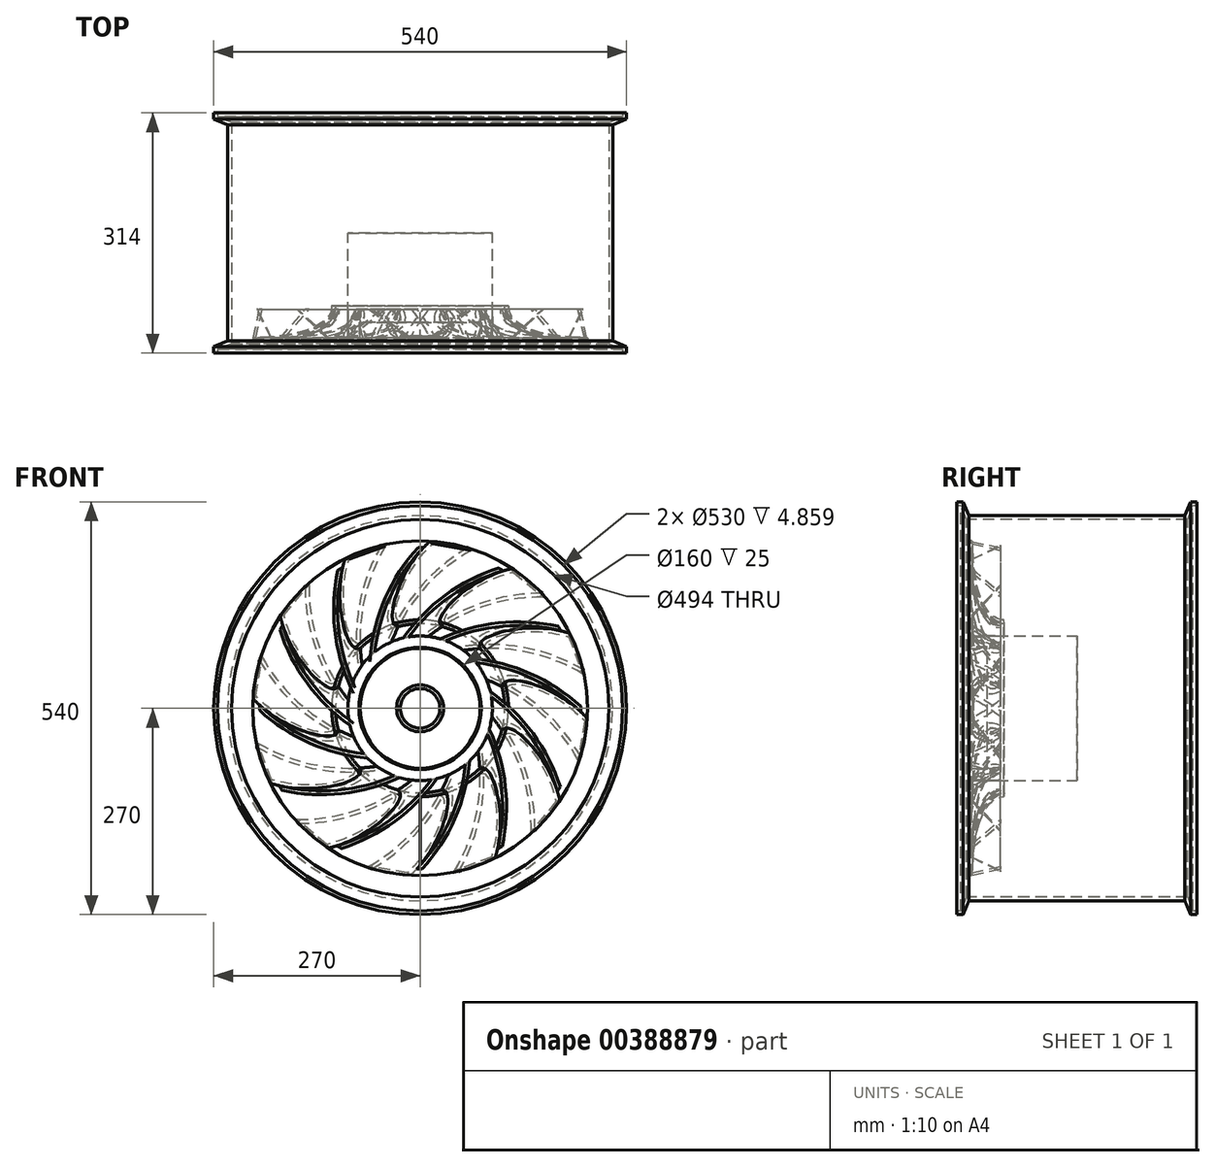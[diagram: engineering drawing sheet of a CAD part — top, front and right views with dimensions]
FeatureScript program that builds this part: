
annotation { "Feature Type Name" : "Feature", "Feature Type Description" : "" }
export const myFeature = defineFeature(function(context is Context, id is Id, definition is map)
    precondition{}
    {
        {
            var Q0;
            Q0=qCreatedBy(makeId("Right.planeOp"),FACE);
            var sketch = newSketch(context, id + "F0", { "sketchPlane" : qUnion([Q0])});
            skLineSegment(sketch, "E0", {"start": v(-157, 265) * mm, "end": v(-152.14, 265) * mm});
            skLineSegment(sketch, "E1", {"start": v(-152.14, 265) * mm, "end": v(-144.8, 247) * mm});
            skLineSegment(sketch, "E2", {"start": v(-144.8, 247) * mm, "end": v(0, 247) * mm});
            skLineSegment(sketch, "E3.0", {"start": v(-141.45, 252) * mm, "end": v(0, 252) * mm});
            skLineSegment(sketch, "E3.1", {"start": v(-148.78, 270) * mm, "end": v(-141.45, 252) * mm});
            skLineSegment(sketch, "E3.2", {"start": v(-157, 270) * mm, "end": v(-148.78, 270) * mm});
            skLineSegment(sketch, "E4", {"start": v(-157, 270) * mm, "end": v(-157, 265) * mm});
            skLineSegment(sketch, "E5", {"start": v(0, 298.63) * mm, "end": v(0, -252.46) * mm, "construction": true});
            skLineSegment(sketch, "E6", {"start": v(-294.47, 0) * mm, "end": v(276.15, 0) * mm, "construction": true});
            skLineSegment(sketch, "E7.MirrorCS", {"start": v(157, 270) * mm, "end": v(148.78, 270) * mm});
            skLineSegment(sketch, "E8.MirrorCS", {"start": v(157, 270) * mm, "end": v(157, 265) * mm});
            skLineSegment(sketch, "E9.MirrorCS", {"start": v(157, 265) * mm, "end": v(152.14, 265) * mm});
            skLineSegment(sketch, "E10.MirrorCS", {"start": v(148.78, 270) * mm, "end": v(141.45, 252) * mm});
            skLineSegment(sketch, "E11.MirrorCS", {"start": v(152.14, 265) * mm, "end": v(144.8, 247) * mm});
            skLineSegment(sketch, "E12.MirrorCS", {"start": v(144.8, 247) * mm, "end": v(0, 247) * mm});
            skLineSegment(sketch, "E13.MirrorCS", {"start": v(141.45, 252) * mm, "end": v(0, 252) * mm});
            skSolve(sketch);
        }
        {
            var Q0;
            Q0 = qSketchRegion(id + "F0", true);
            var Q1;
            Q1=sQuery(id+"F0.wireOp",EDGE,"E6");
            revolve(context, id + "F1", {"entities" : qUnion([Q0]), "axis" : qUnion([Q1]), "revolveType" : RevolveType.FULL});
        }
        {
            var Q0;
            Q0=qCreatedBy(makeId("Front.planeOp"),FACE);
            var sketch = newSketch(context, id + "F2", { "sketchPlane" : qUnion([Q0])});
            skCircle(sketch, "E14", {"center": v(0, 0) * mm, "radius": 94.6 * mm});
            skSolve(sketch);
        }
        {
            var Q0;
            Q0 = qSketchRegion(id + "F2", true);
            extrude(context, id + "F3", {"entities" : qUnion([Q0]), "depth" : 142 * mm});
        }
        {
            var Q0;
            Q0=qCreatedBy(makeId("Front.planeOp"),FACE);
            cPlane(context, id + "F4", {"entities" : qUnion([Q0]), "cplaneType" : CPlaneType.OFFSET, "offset" : 100 * mm, "width" : 150 * mm, "height" : 150 * mm});
        }
        {
            var Q0;
            Q0=qCreatedBy(id+"F4.planeOp",FACE);
            var sketch = newSketch(context, id + "F5", { "sketchPlane" : qUnion([Q0])});
            skArc(sketch, "E15", {"start": v(-55.5, 40.57) * mm, "mid": v(-15.2, 138.78) * mm, "end": v(63.24, 210.31) * mm});
            skArc(sketch, "E16.0", {"start": v(-50.14, 42.17) * mm, "mid": v(-10, 137.48) * mm, "end": v(66.9, 206.64) * mm});
            skLineSegment(sketch, "E17", {"start": v(66.9, 206.64) * mm, "end": v(63.24, 210.31) * mm});
            skLineSegment(sketch, "E18", {"start": v(-50.14, 42.17) * mm, "end": v(-55.5, 40.57) * mm});
            skLineSegment(sketch, "E19.1.0", {"start": v(-45.38, 212.4) * mm, "end": v(-50.39, 213.75) * mm});
            skArc(sketch, "E19.1.1", {"start": v(-64.5, 11.44) * mm, "mid": v(-77.4, 114.06) * mm, "end": v(-45.38, 212.4) * mm});
            skArc(sketch, "E19.1.2", {"start": v(-68.35, 7.39) * mm, "mid": v(-82.55, 112.59) * mm, "end": v(-50.39, 213.75) * mm});
            skLineSegment(sketch, "E19.1.3", {"start": v(-64.5, 11.44) * mm, "end": v(-68.35, 7.39) * mm});
            skLineSegment(sketch, "E19.2.0", {"start": v(-145.5, 161.25) * mm, "end": v(-150.52, 159.92) * mm});
            skArc(sketch, "E19.2.1", {"start": v(-61.59, -22.34) * mm, "mid": v(-124.06, 60.08) * mm, "end": v(-145.5, 161.25) * mm});
            skArc(sketch, "E19.2.2", {"start": v(-62.89, -27.78) * mm, "mid": v(-127.79, 56.23) * mm, "end": v(-150.52, 159.92) * mm});
            skLineSegment(sketch, "E19.2.3", {"start": v(-61.59, -22.34) * mm, "end": v(-62.89, -27.78) * mm});
            skLineSegment(sketch, "E19.3.0", {"start": v(-206.64, 66.9) * mm, "end": v(-210.31, 63.24) * mm});
            skArc(sketch, "E19.3.1", {"start": v(-42.17, -50.14) * mm, "mid": v(-137.48, -10) * mm, "end": v(-206.64, 66.9) * mm});
            skArc(sketch, "E19.3.2", {"start": v(-40.57, -55.5) * mm, "mid": v(-138.78, -15.2) * mm, "end": v(-210.31, 63.24) * mm});
            skLineSegment(sketch, "E19.3.3", {"start": v(-42.17, -50.14) * mm, "end": v(-40.57, -55.5) * mm});
            skLineSegment(sketch, "E19.4.0", {"start": v(-212.4, -45.38) * mm, "end": v(-213.75, -50.39) * mm});
            skArc(sketch, "E19.4.1", {"start": v(-11.44, -64.5) * mm, "mid": v(-114.06, -77.4) * mm, "end": v(-212.4, -45.38) * mm});
            skArc(sketch, "E19.4.2", {"start": v(-7.39, -68.35) * mm, "mid": v(-112.59, -82.55) * mm, "end": v(-213.75, -50.39) * mm});
            skLineSegment(sketch, "E19.4.3", {"start": v(-11.44, -64.5) * mm, "end": v(-7.39, -68.35) * mm});
            skLineSegment(sketch, "E19.5.0", {"start": v(-161.25, -145.5) * mm, "end": v(-159.92, -150.52) * mm});
            skArc(sketch, "E19.5.1", {"start": v(22.34, -61.59) * mm, "mid": v(-60.08, -124.06) * mm, "end": v(-161.25, -145.5) * mm});
            skArc(sketch, "E19.5.2", {"start": v(27.78, -62.89) * mm, "mid": v(-56.23, -127.79) * mm, "end": v(-159.92, -150.52) * mm});
            skLineSegment(sketch, "E19.5.3", {"start": v(22.34, -61.59) * mm, "end": v(27.78, -62.89) * mm});
            skLineSegment(sketch, "E19.6.0", {"start": v(-66.9, -206.64) * mm, "end": v(-63.24, -210.31) * mm});
            skArc(sketch, "E19.6.1", {"start": v(50.14, -42.17) * mm, "mid": v(10, -137.48) * mm, "end": v(-66.9, -206.64) * mm});
            skArc(sketch, "E19.6.2", {"start": v(55.5, -40.57) * mm, "mid": v(15.2, -138.78) * mm, "end": v(-63.24, -210.31) * mm});
            skLineSegment(sketch, "E19.6.3", {"start": v(50.14, -42.17) * mm, "end": v(55.5, -40.57) * mm});
            skLineSegment(sketch, "E19.7.0", {"start": v(45.38, -212.4) * mm, "end": v(50.39, -213.75) * mm});
            skArc(sketch, "E19.7.1", {"start": v(64.5, -11.44) * mm, "mid": v(77.4, -114.06) * mm, "end": v(45.38, -212.4) * mm});
            skArc(sketch, "E19.7.2", {"start": v(68.35, -7.39) * mm, "mid": v(82.55, -112.59) * mm, "end": v(50.39, -213.75) * mm});
            skLineSegment(sketch, "E19.7.3", {"start": v(64.5, -11.44) * mm, "end": v(68.35, -7.39) * mm});
            skLineSegment(sketch, "E19.8.0", {"start": v(145.5, -161.25) * mm, "end": v(150.52, -159.92) * mm});
            skArc(sketch, "E19.8.1", {"start": v(61.59, 22.34) * mm, "mid": v(124.06, -60.08) * mm, "end": v(145.5, -161.25) * mm});
            skArc(sketch, "E19.8.2", {"start": v(62.89, 27.78) * mm, "mid": v(127.79, -56.23) * mm, "end": v(150.52, -159.92) * mm});
            skLineSegment(sketch, "E19.8.3", {"start": v(61.59, 22.34) * mm, "end": v(62.89, 27.78) * mm});
            skLineSegment(sketch, "E19.9.0", {"start": v(206.64, -66.9) * mm, "end": v(210.31, -63.24) * mm});
            skArc(sketch, "E19.9.1", {"start": v(42.17, 50.14) * mm, "mid": v(137.48, 10) * mm, "end": v(206.64, -66.9) * mm});
            skArc(sketch, "E19.9.2", {"start": v(40.57, 55.5) * mm, "mid": v(138.78, 15.2) * mm, "end": v(210.31, -63.24) * mm});
            skLineSegment(sketch, "E19.9.3", {"start": v(42.17, 50.14) * mm, "end": v(40.57, 55.5) * mm});
            skLineSegment(sketch, "E19.10.0", {"start": v(212.4, 45.38) * mm, "end": v(213.75, 50.39) * mm});
            skArc(sketch, "E19.10.1", {"start": v(11.44, 64.5) * mm, "mid": v(114.06, 77.4) * mm, "end": v(212.4, 45.38) * mm});
            skArc(sketch, "E19.10.2", {"start": v(7.39, 68.35) * mm, "mid": v(112.59, 82.55) * mm, "end": v(213.75, 50.39) * mm});
            skLineSegment(sketch, "E19.10.3", {"start": v(11.44, 64.5) * mm, "end": v(7.39, 68.35) * mm});
            skLineSegment(sketch, "E19.11.0", {"start": v(161.25, 145.5) * mm, "end": v(159.92, 150.52) * mm});
            skArc(sketch, "E19.11.1", {"start": v(-22.34, 61.59) * mm, "mid": v(60.08, 124.06) * mm, "end": v(161.25, 145.5) * mm});
            skArc(sketch, "E19.11.2", {"start": v(-27.78, 62.89) * mm, "mid": v(56.23, 127.79) * mm, "end": v(159.92, 150.52) * mm});
            skLineSegment(sketch, "E19.11.3", {"start": v(-22.34, 61.59) * mm, "end": v(-27.78, 62.89) * mm});
            skPoint(sketch, "E19.center", {"position": v(0, 0) * mm});
            skSolve(sketch);
        }
        {
            var Q0;
            Q0=makeQuery(id+"F3.opExtrude","CAP_FACE",FACE,{"disambiguationData":[OSD([sQuery(id+"F2.wireOp",EDGE,"E14")])],"isStart":false});
            var sketch = newSketch(context, id + "F6", { "sketchPlane" : qUnion([Q0])});
            skArc(sketch, "E20", {"start": v(-43.6, 52.71) * mm, "mid": v(20.74, 137.14) * mm, "end": v(115.02, 185.93) * mm});
            skArc(sketch, "E21.0", {"start": v(-38.02, 52.86) * mm, "mid": v(25.42, 134.54) * mm, "end": v(117.6, 181.44) * mm});
            skLineSegment(sketch, "E22", {"start": v(117.6, 181.44) * mm, "end": v(115.02, 185.93) * mm});
            skLineSegment(sketch, "E23", {"start": v(-38.02, 52.86) * mm, "end": v(-43.6, 52.71) * mm});
            skLineSegment(sketch, "E24.1.0", {"start": v(10.64, 216.07) * mm, "end": v(6.15, 218.67) * mm});
            skArc(sketch, "E24.1.1", {"start": v(-59.85, 26.9) * mm, "mid": v(-45.74, 129.36) * mm, "end": v(10.64, 216.07) * mm});
            skArc(sketch, "E24.1.2", {"start": v(-64.6, 23.98) * mm, "mid": v(-51.1, 129.27) * mm, "end": v(6.15, 218.67) * mm});
            skLineSegment(sketch, "E24.1.3", {"start": v(-59.85, 26.9) * mm, "end": v(-64.6, 23.98) * mm});
            skLineSegment(sketch, "E24.2.0", {"start": v(-99.3, 192.57) * mm, "end": v(-104.5, 192.58) * mm});
            skArc(sketch, "E24.2.1", {"start": v(-65.77, -6.49) * mm, "mid": v(-104.78, 89.3) * mm, "end": v(-99.3, 192.57) * mm});
            skArc(sketch, "E24.2.2", {"start": v(-68.43, -11.4) * mm, "mid": v(-109.38, 86.54) * mm, "end": v(-104.5, 192.58) * mm});
            skLineSegment(sketch, "E24.2.3", {"start": v(-65.77, -6.49) * mm, "end": v(-68.43, -11.4) * mm});
            skLineSegment(sketch, "E24.3.0", {"start": v(-182.78, 117.26) * mm, "end": v(-187.28, 114.67) * mm});
            skArc(sketch, "E24.3.1", {"start": v(-54.2, -38.37) * mm, "mid": v(-135.88, 25.08) * mm, "end": v(-182.78, 117.26) * mm});
            skArc(sketch, "E24.3.2", {"start": v(-54.05, -43.95) * mm, "mid": v(-138.49, 20.4) * mm, "end": v(-187.28, 114.67) * mm});
            skLineSegment(sketch, "E24.3.3", {"start": v(-54.2, -38.37) * mm, "end": v(-54.05, -43.95) * mm});
            skLineSegment(sketch, "E24.4.0", {"start": v(-217.41, 10.3) * mm, "end": v(-220.01, 5.8) * mm});
            skArc(sketch, "E24.4.1", {"start": v(-28.25, -60.2) * mm, "mid": v(-130.7, -46.09) * mm, "end": v(-217.41, 10.3) * mm});
            skArc(sketch, "E24.4.2", {"start": v(-25.33, -64.95) * mm, "mid": v(-130.62, -51.45) * mm, "end": v(-220.01, 5.8) * mm});
            skLineSegment(sketch, "E24.4.3", {"start": v(-28.25, -60.2) * mm, "end": v(-25.33, -64.95) * mm});
            skLineSegment(sketch, "E24.5.0", {"start": v(-193.92, -99.66) * mm, "end": v(-193.93, -104.84) * mm});
            skArc(sketch, "E24.5.1", {"start": v(5.14, -66.12) * mm, "mid": v(-90.64, -105.13) * mm, "end": v(-193.92, -99.66) * mm});
            skArc(sketch, "E24.5.2", {"start": v(10.06, -68.78) * mm, "mid": v(-87.89, -109.73) * mm, "end": v(-193.93, -104.84) * mm});
            skLineSegment(sketch, "E24.5.3", {"start": v(5.14, -66.12) * mm, "end": v(10.06, -68.78) * mm});
            skLineSegment(sketch, "E24.6.0", {"start": v(-118.6, -183.13) * mm, "end": v(-116.02, -187.62) * mm});
            skArc(sketch, "E24.6.1", {"start": v(37.02, -54.55) * mm, "mid": v(-26.42, -136.23) * mm, "end": v(-118.6, -183.13) * mm});
            skArc(sketch, "E24.6.2", {"start": v(42.6, -54.4) * mm, "mid": v(-21.74, -138.83) * mm, "end": v(-116.02, -187.62) * mm});
            skLineSegment(sketch, "E24.6.3", {"start": v(37.02, -54.55) * mm, "end": v(42.6, -54.4) * mm});
            skLineSegment(sketch, "E24.7.0", {"start": v(-11.64, -217.76) * mm, "end": v(-7.15, -220.36) * mm});
            skArc(sketch, "E24.7.1", {"start": v(58.85, -28.6) * mm, "mid": v(44.74, -131.05) * mm, "end": v(-11.64, -217.76) * mm});
            skArc(sketch, "E24.7.2", {"start": v(63.61, -25.67) * mm, "mid": v(50.1, -130.96) * mm, "end": v(-7.15, -220.36) * mm});
            skLineSegment(sketch, "E24.7.3", {"start": v(58.85, -28.6) * mm, "end": v(63.61, -25.67) * mm});
            skLineSegment(sketch, "E24.8.0", {"start": v(98.31, -194.26) * mm, "end": v(103.5, -194.27) * mm});
            skArc(sketch, "E24.8.1", {"start": v(64.77, 4.8) * mm, "mid": v(103.78, -90.99) * mm, "end": v(98.31, -194.26) * mm});
            skArc(sketch, "E24.8.2", {"start": v(67.44, 9.7) * mm, "mid": v(108.38, -88.23) * mm, "end": v(103.5, -194.27) * mm});
            skLineSegment(sketch, "E24.8.3", {"start": v(64.77, 4.8) * mm, "end": v(67.44, 9.7) * mm});
            skLineSegment(sketch, "E24.9.0", {"start": v(181.78, -118.95) * mm, "end": v(186.28, -116.36) * mm});
            skArc(sketch, "E24.9.1", {"start": v(53.2, 36.68) * mm, "mid": v(134.88, -26.77) * mm, "end": v(181.78, -118.95) * mm});
            skArc(sketch, "E24.9.2", {"start": v(53.06, 42.26) * mm, "mid": v(137.49, -22.08) * mm, "end": v(186.28, -116.36) * mm});
            skLineSegment(sketch, "E24.9.3", {"start": v(53.2, 36.68) * mm, "end": v(53.06, 42.26) * mm});
            skLineSegment(sketch, "E24.10.0", {"start": v(216.41, -11.98) * mm, "end": v(219.01, -7.5) * mm});
            skArc(sketch, "E24.10.1", {"start": v(27.25, 58.5) * mm, "mid": v(129.7, 44.4) * mm, "end": v(216.41, -11.98) * mm});
            skArc(sketch, "E24.10.2", {"start": v(24.33, 63.27) * mm, "mid": v(129.62, 49.76) * mm, "end": v(219.01, -7.5) * mm});
            skLineSegment(sketch, "E24.10.3", {"start": v(27.25, 58.5) * mm, "end": v(24.33, 63.27) * mm});
            skLineSegment(sketch, "E24.11.0", {"start": v(192.92, 97.97) * mm, "end": v(192.93, 103.15) * mm});
            skArc(sketch, "E24.11.1", {"start": v(-6.14, 64.43) * mm, "mid": v(89.64, 103.44) * mm, "end": v(192.92, 97.97) * mm});
            skArc(sketch, "E24.11.2", {"start": v(-11.05, 67.09) * mm, "mid": v(86.89, 108.04) * mm, "end": v(192.93, 103.15) * mm});
            skLineSegment(sketch, "E24.11.3", {"start": v(-6.14, 64.43) * mm, "end": v(-11.05, 67.09) * mm});
            skPoint(sketch, "E24.center", {"position": v(-0.5, -0.84) * mm});
            skSolve(sketch);
        }
        {
            var Q1;
            {var subQ0=sQuery(id+"F6.wireOp",EDGE,"E24.2.0");Q1=makeQuery(id+"F6.imprint","IMPRINT",FACE,{"disambiguationData":[TD([[makeQuery(id+"F6.imprint","IMPRINT",EDGE,{"derivedFrom":subQ0}),1.0]])]});}
            var Q2;
            Q2=makeQuery(id+"F5.imprint","IMPRINT",FACE,{"disambiguationData":[TD([[makeQuery(id+"F5.imprint","IMPRINT",EDGE,{"derivedFrom":sQuery(id+"F5.wireOp",EDGE,"E19.1.0")}),1.0]])]});
            loft(context, id + "F7", {"sheetProfilesArray" : [{ "sheetProfileEntities" : qUnion([Q1]) }, { "sheetProfileEntities" : qUnion([Q2]) }]});
        }
        {
            var Q0;
            {var subQ0=sQuery(id+"F6.wireOp",EDGE,"E24.2.0");Q0=makeQuery(id+"F7.opLoft","SWEPT_BODY",BODY,{"disambiguationData":[OSD([makeQuery(id+"F5.imprint","IMPRINT",FACE,{"disambiguationData":[TD([[makeQuery(id+"F5.imprint","IMPRINT",EDGE,{"derivedFrom":sQuery(id+"F5.wireOp",EDGE,"E19.1.0")}),1.0]])]}),makeQuery(id+"F6.imprint","IMPRINT",FACE,{"disambiguationData":[TD([[makeQuery(id+"F6.imprint","IMPRINT",EDGE,{"derivedFrom":subQ0}),1.0]])]})])]});}
            var Q1;
            Q1=sQuery(id+"F0.wireOp",EDGE,"E6");
            circularPattern(context, id + "F8", {"operationType" : NewBodyOperationType.ADD, "entities" : qUnion([Q0]), "axis" : qUnion([Q1]), "angle" : 360 * degree, "instanceCount" : 12, "equalSpace" : true, "computeTransformsWithoutBuiltin" : true});
        }
        {
            var Q0;
            Q0=qCreatedBy(makeId("Right.planeOp"),FACE);
            var sketch = newSketch(context, id + "F9", { "sketchPlane" : qUnion([Q0])});
            skFitSpline(sketch, "E25", {"points": [v(-142.34, 219.16) * mm, v(-95.31, 110.7) * mm], "startDerivative": vector(5.55, -196.37) * mm, "endDerivative": vector(88.39, 0.05) * mm});
            skFitSpline(sketch, "E26.0", {"points": [v(-137.35, 219.3) * mm, v(-137.12, 211.21) * mm, v(-136.23, 195.75) * mm, v(-133.63, 174.97) * mm, v(-129.79, 156.87) * mm, v(-124.75, 141.74) * mm, v(-119.63, 131.87) * mm, v(-115.1, 125.73) * mm, v(-111.52, 122.01) * mm, v(-107.79, 119.18) * mm, v(-103.9, 117.18) * mm, v(-99.8, 115.98) * mm, v(-96.85, 115.7) * mm, v(-95.32, 115.7) * mm]});
            skLineSegment(sketch, "E27", {"start": v(-137.34, 219.02) * mm, "end": v(-142.34, 219.16) * mm});
            skLineSegment(sketch, "E28", {"start": v(-95.31, 110.7) * mm, "end": v(-95.5, 115.7) * mm});
            skSolve(sketch);
        }
        {
            var Q0;
            Q0 = qSketchRegion(id + "F9", true);
            var Q1;
            Q1=sQuery(id+"F0.wireOp",EDGE,"E6");
            revolve(context, id + "F10", {"operationType" : NewBodyOperationType.ADD, "entities" : qUnion([Q0]), "axis" : qUnion([Q1]), "revolveType" : RevolveType.FULL});
        }
        {
            var Q0;
            {var subQ1=sQuery(id+"F6.wireOp",EDGE,"E24.2.0");var subQ2=sQuery(id+"F5.wireOp",EDGE,"E19.1.3");var subQ3=sQuery(id+"F5.wireOp",EDGE,"E19.1.0");var subQ4=sQuery(id+"F2.wireOp",EDGE,"E14");var subQ5=sQuery(id+"F6.wireOp",EDGE,"E24.2.1");var subQ6=makeQuery(id+"F3.opExtrude","CAP_EDGE",EDGE,{"disambiguationData":[OSD([subQ4])],"isStart":false});Q0=makeQuery(id+"F8.boolean.opBoolean","SPLIT",EDGE,{"disambiguationData":[TD([makeQuery(id+"F8.opPattern","COPY",FACE,{"derivedFrom":makeQuery(id+"F7.opLoft","SWEPT_FACE",FACE,{"disambiguationData":[OSD([subQ4,subQ3,sQuery(id+"F5.wireOp",EDGE,"E19.1.1"),subQ2,subQ1,subQ5])]}),"instanceName":"3"})])],"derivedFrom":subQ6});}
            var Q1;
            {var subQ1=sQuery(id+"F6.wireOp",EDGE,"E24.2.0");var subQ2=sQuery(id+"F5.wireOp",EDGE,"E19.1.3");var subQ3=sQuery(id+"F5.wireOp",EDGE,"E19.1.0");var subQ4=sQuery(id+"F2.wireOp",EDGE,"E14");var subQ5=sQuery(id+"F6.wireOp",EDGE,"E24.2.1");var subQ6=makeQuery(id+"F3.opExtrude","CAP_EDGE",EDGE,{"disambiguationData":[OSD([subQ4])],"isStart":false});Q1=makeQuery(id+"F8.boolean.opBoolean","SPLIT",EDGE,{"disambiguationData":[TD([makeQuery(id+"F8.opPattern","COPY",FACE,{"derivedFrom":makeQuery(id+"F7.opLoft","SWEPT_FACE",FACE,{"disambiguationData":[OSD([subQ4,subQ3,sQuery(id+"F5.wireOp",EDGE,"E19.1.1"),subQ2,subQ1,subQ5])]}),"instanceName":"4"})])],"derivedFrom":subQ6});}
            var Q2;
            {var subQ1=sQuery(id+"F6.wireOp",EDGE,"E24.2.0");var subQ2=sQuery(id+"F5.wireOp",EDGE,"E19.1.3");var subQ3=sQuery(id+"F5.wireOp",EDGE,"E19.1.0");var subQ4=sQuery(id+"F2.wireOp",EDGE,"E14");var subQ5=sQuery(id+"F6.wireOp",EDGE,"E24.2.1");var subQ6=makeQuery(id+"F3.opExtrude","CAP_EDGE",EDGE,{"disambiguationData":[OSD([subQ4])],"isStart":false});Q2=makeQuery(id+"F8.boolean.opBoolean","SPLIT",EDGE,{"disambiguationData":[TD([makeQuery(id+"F8.opPattern","COPY",FACE,{"derivedFrom":makeQuery(id+"F7.opLoft","SWEPT_FACE",FACE,{"disambiguationData":[OSD([subQ4,subQ3,sQuery(id+"F5.wireOp",EDGE,"E19.1.1"),subQ2,subQ1,subQ5])]}),"instanceName":"5"})])],"derivedFrom":subQ6});}
            var Q3;
            {var subQ0=sQuery(id+"F6.wireOp",EDGE,"E24.2.0");var subQ1=sQuery(id+"F6.wireOp",EDGE,"E24.2.1");var subQ2=sQuery(id+"F2.wireOp",EDGE,"E14");var subQ3=makeQuery(id+"F3.opExtrude","CAP_EDGE",EDGE,{"disambiguationData":[OSD([subQ2])],"isStart":false});var subQ8=sQuery(id+"F5.wireOp",EDGE,"E19.1.3");var subQ9=sQuery(id+"F5.wireOp",EDGE,"E19.1.0");Q3=makeQuery(id+"F8.boolean.opBoolean","SPLIT",EDGE,{"disambiguationData":[TD([makeQuery(id+"F8.opPattern","COPY",FACE,{"derivedFrom":makeQuery(id+"F7.opLoft","SWEPT_FACE",FACE,{"disambiguationData":[OSD([subQ2,subQ9,sQuery(id+"F5.wireOp",EDGE,"E19.1.1"),subQ8,subQ0,subQ1])]}),"instanceName":"6"})])],"derivedFrom":subQ3});}
            var Q4;
            {var subQ0=sQuery(id+"F6.wireOp",EDGE,"E24.2.1");var subQ1=sQuery(id+"F6.wireOp",EDGE,"E24.2.0");var subQ2=sQuery(id+"F5.wireOp",EDGE,"E19.1.3");var subQ3=sQuery(id+"F5.wireOp",EDGE,"E19.1.0");var subQ4=sQuery(id+"F2.wireOp",EDGE,"E14");var subQ5=makeQuery(id+"F3.opExtrude","CAP_EDGE",EDGE,{"disambiguationData":[OSD([subQ4])],"isStart":false});Q4=makeQuery(id+"F8.boolean.opBoolean","SPLIT",EDGE,{"disambiguationData":[TD([makeQuery(id+"F8.opPattern","COPY",FACE,{"derivedFrom":makeQuery(id+"F7.opLoft","SWEPT_FACE",FACE,{"disambiguationData":[OSD([subQ4,subQ3,sQuery(id+"F5.wireOp",EDGE,"E19.1.1"),subQ2,subQ1,subQ0])]}),"instanceName":"7"})])],"derivedFrom":subQ5});}
            var Q5;
            {var subQ0=sQuery(id+"F6.wireOp",EDGE,"E24.2.0");var subQ1=sQuery(id+"F6.wireOp",EDGE,"E24.2.1");var subQ2=sQuery(id+"F2.wireOp",EDGE,"E14");var subQ3=makeQuery(id+"F3.opExtrude","CAP_EDGE",EDGE,{"disambiguationData":[OSD([subQ2])],"isStart":false});var subQ8=sQuery(id+"F5.wireOp",EDGE,"E19.1.3");var subQ9=sQuery(id+"F5.wireOp",EDGE,"E19.1.0");Q5=makeQuery(id+"F8.boolean.opBoolean","SPLIT",EDGE,{"disambiguationData":[TD([makeQuery(id+"F8.opPattern","COPY",FACE,{"derivedFrom":makeQuery(id+"F7.opLoft","SWEPT_FACE",FACE,{"disambiguationData":[OSD([subQ2,subQ9,sQuery(id+"F5.wireOp",EDGE,"E19.1.1"),subQ8,subQ0,subQ1])]}),"instanceName":"8"})])],"derivedFrom":subQ3});}
            var Q6;
            {var subQ0=sQuery(id+"F6.wireOp",EDGE,"E24.2.0");var subQ1=sQuery(id+"F6.wireOp",EDGE,"E24.2.1");var subQ2=sQuery(id+"F2.wireOp",EDGE,"E14");var subQ3=makeQuery(id+"F3.opExtrude","CAP_EDGE",EDGE,{"disambiguationData":[OSD([subQ2])],"isStart":false});var subQ8=sQuery(id+"F5.wireOp",EDGE,"E19.1.3");var subQ9=sQuery(id+"F5.wireOp",EDGE,"E19.1.0");Q6=makeQuery(id+"F8.boolean.opBoolean","SPLIT",EDGE,{"disambiguationData":[TD([makeQuery(id+"F8.opPattern","COPY",FACE,{"derivedFrom":makeQuery(id+"F7.opLoft","SWEPT_FACE",FACE,{"disambiguationData":[OSD([subQ2,subQ9,sQuery(id+"F5.wireOp",EDGE,"E19.1.1"),subQ8,subQ0,subQ1])]}),"instanceName":"9"})])],"derivedFrom":subQ3});}
            var Q7;
            {var subQ0=sQuery(id+"F6.wireOp",EDGE,"E24.2.0");var subQ1=sQuery(id+"F6.wireOp",EDGE,"E24.2.1");var subQ2=sQuery(id+"F2.wireOp",EDGE,"E14");var subQ3=makeQuery(id+"F3.opExtrude","CAP_EDGE",EDGE,{"disambiguationData":[OSD([subQ2])],"isStart":false});var subQ8=sQuery(id+"F5.wireOp",EDGE,"E19.1.3");var subQ9=sQuery(id+"F5.wireOp",EDGE,"E19.1.0");Q7=makeQuery(id+"F8.boolean.opBoolean","SPLIT",EDGE,{"disambiguationData":[TD([makeQuery(id+"F8.opPattern","COPY",FACE,{"derivedFrom":makeQuery(id+"F7.opLoft","SWEPT_FACE",FACE,{"disambiguationData":[OSD([subQ2,subQ9,sQuery(id+"F5.wireOp",EDGE,"E19.1.1"),subQ8,subQ0,subQ1])]}),"instanceName":"10"})])],"derivedFrom":subQ3});}
            var Q8;
            {var subQ0=sQuery(id+"F6.wireOp",EDGE,"E24.2.0");var subQ2=sQuery(id+"F2.wireOp",EDGE,"E14");var subQ3=makeQuery(id+"F3.opExtrude","CAP_EDGE",EDGE,{"disambiguationData":[OSD([subQ2])],"isStart":false});var subQ5=sQuery(id+"F6.wireOp",EDGE,"E24.2.2");var subQ8=sQuery(id+"F5.wireOp",EDGE,"E19.1.3");var subQ9=sQuery(id+"F5.wireOp",EDGE,"E19.1.0");Q8=makeQuery(id+"F8.boolean.opBoolean","SPLIT",EDGE,{"disambiguationData":[TD([makeQuery(id+"F7.opLoft","SWEPT_FACE",FACE,{"disambiguationData":[OSD([subQ2,subQ9,sQuery(id+"F5.wireOp",EDGE,"E19.1.2"),subQ8,subQ0,subQ5])]})])],"derivedFrom":subQ3});}
            var Q9;
            {var subQ0=sQuery(id+"F6.wireOp",EDGE,"E24.2.0");var subQ1=sQuery(id+"F6.wireOp",EDGE,"E24.2.1");var subQ2=sQuery(id+"F2.wireOp",EDGE,"E14");var subQ3=makeQuery(id+"F3.opExtrude","CAP_EDGE",EDGE,{"disambiguationData":[OSD([subQ2])],"isStart":false});var subQ8=sQuery(id+"F5.wireOp",EDGE,"E19.1.3");var subQ9=sQuery(id+"F5.wireOp",EDGE,"E19.1.0");Q9=makeQuery(id+"F8.boolean.opBoolean","SPLIT",EDGE,{"disambiguationData":[TD([makeQuery(id+"F7.opLoft","SWEPT_FACE",FACE,{"disambiguationData":[OSD([subQ2,subQ9,sQuery(id+"F5.wireOp",EDGE,"E19.1.1"),subQ8,subQ0,subQ1])]})])],"derivedFrom":subQ3});}
            var Q10;
            {var subQ0=sQuery(id+"F6.wireOp",EDGE,"E24.2.0");var subQ1=sQuery(id+"F6.wireOp",EDGE,"E24.2.1");var subQ2=sQuery(id+"F2.wireOp",EDGE,"E14");var subQ3=makeQuery(id+"F3.opExtrude","CAP_EDGE",EDGE,{"disambiguationData":[OSD([subQ2])],"isStart":false});var subQ8=sQuery(id+"F5.wireOp",EDGE,"E19.1.3");var subQ9=sQuery(id+"F5.wireOp",EDGE,"E19.1.0");Q10=makeQuery(id+"F8.boolean.opBoolean","SPLIT",EDGE,{"disambiguationData":[TD([makeQuery(id+"F8.opPattern","COPY",FACE,{"derivedFrom":makeQuery(id+"F7.opLoft","SWEPT_FACE",FACE,{"disambiguationData":[OSD([subQ2,subQ9,sQuery(id+"F5.wireOp",EDGE,"E19.1.1"),subQ8,subQ0,subQ1])]}),"instanceName":"1"})])],"derivedFrom":subQ3});}
            var Q11;
            {var subQ0=sQuery(id+"F6.wireOp",EDGE,"E24.2.0");var subQ1=sQuery(id+"F6.wireOp",EDGE,"E24.2.1");var subQ2=sQuery(id+"F2.wireOp",EDGE,"E14");var subQ3=makeQuery(id+"F3.opExtrude","CAP_EDGE",EDGE,{"disambiguationData":[OSD([subQ2])],"isStart":false});var subQ8=sQuery(id+"F5.wireOp",EDGE,"E19.1.3");var subQ9=sQuery(id+"F5.wireOp",EDGE,"E19.1.0");Q11=makeQuery(id+"F8.boolean.opBoolean","SPLIT",EDGE,{"disambiguationData":[TD([makeQuery(id+"F8.opPattern","COPY",FACE,{"derivedFrom":makeQuery(id+"F7.opLoft","SWEPT_FACE",FACE,{"disambiguationData":[OSD([subQ2,subQ9,sQuery(id+"F5.wireOp",EDGE,"E19.1.1"),subQ8,subQ0,subQ1])]}),"instanceName":"2"})])],"derivedFrom":subQ3});}
            fillet(context, id + "F11", {"entities" : qUnion([Q0, Q1, Q2, Q3, Q4, Q5, Q6, Q7, Q8, Q9, Q10, Q11]), "radius" : 5 * mm, "tangentPropagation" : true, "allowEdgeOverflow" : false});
        }
        {
            var Q0;
            {var subQ0=sQuery(id+"F6.wireOp",EDGE,"E24.2.2");var subQ1=sQuery(id+"F6.wireOp",EDGE,"E24.2.0");var subQ2=sQuery(id+"F5.wireOp",EDGE,"E19.1.3");var subQ3=sQuery(id+"F5.wireOp",EDGE,"E19.1.2");var subQ4=sQuery(id+"F5.wireOp",EDGE,"E19.1.0");var subQ5=sQuery(id+"F2.wireOp",EDGE,"E14");var subQ6=makeQuery(id+"F7.opLoft","SWEPT_FACE",FACE,{"disambiguationData":[OSD([subQ5,subQ4,subQ3,subQ2,subQ1,subQ0])]});var subQ7=sQuery(id+"F6.wireOp",EDGE,"E24.2.1");var subQ8=sQuery(id+"F5.wireOp",EDGE,"E19.1.1");var subQ9=makeQuery(id+"F7.opLoft","SWEPT_FACE",FACE,{"disambiguationData":[OSD([subQ5,subQ4,subQ8,subQ2,subQ1,subQ7])]});var subQ10=makeQuery(id+"F7.opLoft","SWEPT_FACE",FACE,{"disambiguationData":[OSD([subQ4,subQ8,subQ3,subQ1,subQ7,subQ0])]});var subQ14=makeQuery(id+"F7.opLoft","CAP_FACE",FACE,{"disambiguationData":[OSD([makeQuery(id+"F6.imprint","IMPRINT",FACE,{"disambiguationData":[TD([[makeQuery(id+"F6.imprint","IMPRINT",EDGE,{"derivedFrom":subQ1}),1.0]])]})])],"isStart":true});Q0=makeQuery(id+"F10.boolean.opBoolean","SPLIT",FACE,{"disambiguationData":[TD([makeQuery(id+"F3.opExtrude","SWEPT_FACE",FACE,{"disambiguationData":[OSD([subQ5])]}),subQ10,subQ9,subQ6,makeQuery(id+"F8.opPattern","COPY",FACE,{"derivedFrom":subQ10,"instanceName":"1"}),makeQuery(id+"F8.opPattern","COPY",FACE,{"derivedFrom":subQ9,"instanceName":"1"}),makeQuery(id+"F8.opPattern","COPY",FACE,{"derivedFrom":subQ6,"instanceName":"1"}),makeQuery(id+"F8.opPattern","COPY",FACE,{"derivedFrom":subQ10,"instanceName":"2"}),makeQuery(id+"F8.opPattern","COPY",FACE,{"derivedFrom":subQ9,"instanceName":"2"}),makeQuery(id+"F8.opPattern","COPY",FACE,{"derivedFrom":subQ6,"instanceName":"2"}),makeQuery(id+"F8.opPattern","COPY",FACE,{"derivedFrom":subQ10,"instanceName":"3"}),makeQuery(id+"F8.opPattern","COPY",FACE,{"derivedFrom":subQ9,"instanceName":"3"}),makeQuery(id+"F8.opPattern","COPY",FACE,{"derivedFrom":subQ6,"instanceName":"3"}),makeQuery(id+"F8.opPattern","COPY",FACE,{"derivedFrom":subQ10,"instanceName":"4"}),makeQuery(id+"F8.opPattern","COPY",FACE,{"derivedFrom":subQ9,"instanceName":"4"}),makeQuery(id+"F8.opPattern","COPY",FACE,{"derivedFrom":subQ6,"instanceName":"4"}),makeQuery(id+"F8.opPattern","COPY",FACE,{"derivedFrom":subQ10,"instanceName":"5"}),makeQuery(id+"F8.opPattern","COPY",FACE,{"derivedFrom":subQ9,"instanceName":"5"}),makeQuery(id+"F8.opPattern","COPY",FACE,{"derivedFrom":subQ6,"instanceName":"5"}),makeQuery(id+"F8.opPattern","COPY",FACE,{"derivedFrom":subQ10,"instanceName":"6"}),makeQuery(id+"F8.opPattern","COPY",FACE,{"derivedFrom":subQ9,"instanceName":"6"}),makeQuery(id+"F8.opPattern","COPY",FACE,{"derivedFrom":subQ6,"instanceName":"6"}),makeQuery(id+"F8.opPattern","COPY",FACE,{"derivedFrom":subQ10,"instanceName":"7"}),makeQuery(id+"F8.opPattern","COPY",FACE,{"derivedFrom":subQ9,"instanceName":"7"}),makeQuery(id+"F8.opPattern","COPY",FACE,{"derivedFrom":subQ6,"instanceName":"7"}),makeQuery(id+"F8.opPattern","COPY",FACE,{"derivedFrom":subQ10,"instanceName":"8"}),makeQuery(id+"F8.opPattern","COPY",FACE,{"derivedFrom":subQ9,"instanceName":"8"}),makeQuery(id+"F8.opPattern","COPY",FACE,{"derivedFrom":subQ6,"instanceName":"8"}),makeQuery(id+"F8.opPattern","COPY",FACE,{"derivedFrom":subQ10,"instanceName":"9"}),makeQuery(id+"F8.opPattern","COPY",FACE,{"derivedFrom":subQ9,"instanceName":"9"}),makeQuery(id+"F8.opPattern","COPY",FACE,{"derivedFrom":subQ6,"instanceName":"9"}),makeQuery(id+"F8.opPattern","COPY",FACE,{"derivedFrom":subQ10,"instanceName":"10"}),makeQuery(id+"F8.opPattern","COPY",FACE,{"derivedFrom":subQ9,"instanceName":"10"}),makeQuery(id+"F8.opPattern","COPY",FACE,{"derivedFrom":subQ6,"instanceName":"10"}),makeQuery(id+"F8.opPattern","COPY",FACE,{"derivedFrom":subQ10,"instanceName":"11"}),makeQuery(id+"F8.opPattern","COPY",FACE,{"derivedFrom":subQ9,"instanceName":"11"}),makeQuery(id+"F8.opPattern","COPY",FACE,{"derivedFrom":subQ6,"instanceName":"11"}),makeQuery(id+"F10.opRevolve","SWEPT_FACE",FACE,{"disambiguationData":[OSD([sQuery(id+"F9.wireOp",EDGE,"E25")])]})])],"derivedFrom":makeQuery(id+"F8.boolean.opBoolean","MERGE",FACE,{"derivedFrom":[makeQuery(id+"F3.opExtrude","CAP_FACE",FACE,{"disambiguationData":[OSD([subQ5])],"isStart":false}),subQ14,makeQuery(id+"F8.opPattern","COPY",FACE,{"derivedFrom":subQ14,"instanceName":"1"}),makeQuery(id+"F8.opPattern","COPY",FACE,{"derivedFrom":subQ14,"instanceName":"2"}),makeQuery(id+"F8.opPattern","COPY",FACE,{"derivedFrom":subQ14,"instanceName":"3"}),makeQuery(id+"F8.opPattern","COPY",FACE,{"derivedFrom":subQ14,"instanceName":"4"}),makeQuery(id+"F8.opPattern","COPY",FACE,{"derivedFrom":subQ14,"instanceName":"5"}),makeQuery(id+"F8.opPattern","COPY",FACE,{"derivedFrom":subQ14,"instanceName":"6"}),makeQuery(id+"F8.opPattern","COPY",FACE,{"derivedFrom":subQ14,"instanceName":"7"}),makeQuery(id+"F8.opPattern","COPY",FACE,{"derivedFrom":subQ14,"instanceName":"8"}),makeQuery(id+"F8.opPattern","COPY",FACE,{"derivedFrom":subQ14,"instanceName":"9"}),makeQuery(id+"F8.opPattern","COPY",FACE,{"derivedFrom":subQ14,"instanceName":"10"}),makeQuery(id+"F8.opPattern","COPY",FACE,{"derivedFrom":subQ14,"instanceName":"11"})]})});}
            var sketch = newSketch(context, id + "F12", { "sketchPlane" : qUnion([Q0])});
            skCircle(sketch, "E29", {"center": v(0, 0) * mm, "radius": 80 * mm});
            skSolve(sketch);
        }
        {
            var Q0;
            Q0 = qSketchRegion(id + "F12", true);
            extrude(context, id + "F13", {"entities" : qUnion([Q0]), "operationType" : NewBodyOperationType.REMOVE, "oppositeDirection" : true, "depth" : 25 * mm});
        }
        {
            var Q0;
            Q0=makeQuery(id+"F13.boolean.opBoolean","COPY",FACE,{"derivedFrom":makeQuery(id+"F13.opExtrude","CAP_FACE",FACE,{"disambiguationData":[OSD([sQuery(id+"F12.wireOp",EDGE,"E29")])],"isStart":false})});
            var sketch = newSketch(context, id + "F14", { "sketchPlane" : qUnion([Q0])});
            skCircle(sketch, "E30", {"center": v(0, 0) * mm, "radius": 78.5 * mm});
            skSolve(sketch);
        }
        {
            var Q0;
            Q0 = qSketchRegion(id + "F14", true);
            extrude(context, id + "F15", {"entities" : qUnion([Q0]), "operationType" : NewBodyOperationType.ADD, "depth" : 25 * mm});
        }
        {
            var Q0;
            Q0=makeQuery(id+"F15.opExtrude","CAP_FACE",FACE,{"disambiguationData":[OSD([sQuery(id+"F14.wireOp",EDGE,"E30")])],"isStart":false});
            var sketch = newSketch(context, id + "F16", { "sketchPlane" : qUnion([Q0])});
            skCircle(sketch, "E31", {"center": v(0, 0) * mm, "radius": 30.72 * mm});
            skSolve(sketch);
        }
        {
            var Q0;
            Q0 = qSketchRegion(id + "F16", true);
            extrude(context, id + "F17", {"entities" : qUnion([Q0]), "operationType" : NewBodyOperationType.REMOVE, "oppositeDirection" : true, "depth" : 7 * mm, "hasDraft" : true, "draftAngle" : 35 * degree, "draftPullDirection" : true});
        }
    });
